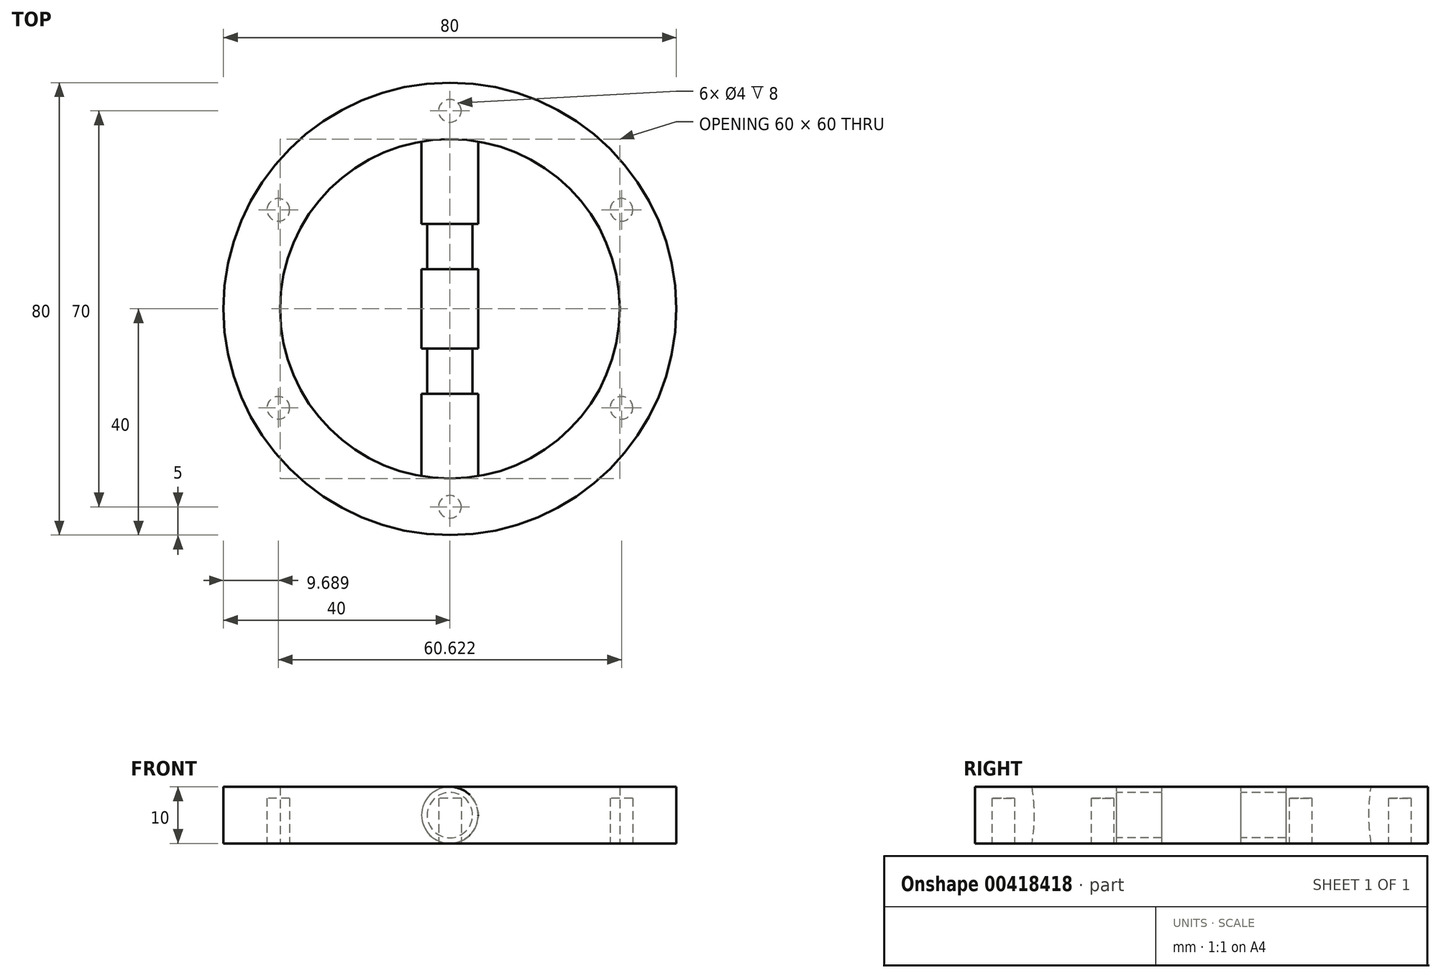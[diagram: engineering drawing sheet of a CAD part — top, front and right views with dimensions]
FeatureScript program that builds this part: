
annotation { "Feature Type Name" : "Feature", "Feature Type Description" : "" }
export const myFeature = defineFeature(function(context is Context, id is Id, definition is map)
    precondition{}
    {
        {
            var Q0;
            Q0=qCreatedBy(makeId("Top.planeOp"),FACE);
            var sketch = newSketch(context, id + "F0", { "sketchPlane" : qUnion([Q0])});
            skCircle(sketch, "E0", {"center": v(0, 0) * mm, "radius": 30 * mm});
            skCircle(sketch, "E1", {"center": v(0, 0) * mm, "radius": 35 * mm, "construction": true});
            skCircle(sketch, "E2", {"center": v(0, 0) * mm, "radius": 40 * mm});
            skLineSegment(sketch, "E3", {"start": v(0, 35) * mm, "end": v(-30.31, -17.5) * mm, "construction": true});
            skLineSegment(sketch, "E4", {"start": v(-30.31, -17.5) * mm, "end": v(30.31, -17.5) * mm, "construction": true});
            skLineSegment(sketch, "E5", {"start": v(30.31, -17.5) * mm, "end": v(0, 35) * mm, "construction": true});
            skLineSegment(sketch, "E6", {"start": v(0, -35) * mm, "end": v(-30.31, 17.5) * mm, "construction": true});
            skLineSegment(sketch, "E7", {"start": v(-30.31, 17.5) * mm, "end": v(30.31, 17.5) * mm, "construction": true});
            skLineSegment(sketch, "E8", {"start": v(30.31, 17.5) * mm, "end": v(0, -35) * mm, "construction": true});
            skCircle(sketch, "E9", {"center": v(0, 35) * mm, "radius": 2 * mm});
            skCircle(sketch, "E10", {"center": v(-30.31, 17.5) * mm, "radius": 2 * mm});
            skCircle(sketch, "E11", {"center": v(-30.31, -17.5) * mm, "radius": 2 * mm});
            skCircle(sketch, "E12", {"center": v(0, -35) * mm, "radius": 2 * mm});
            skCircle(sketch, "E13", {"center": v(30.31, -17.5) * mm, "radius": 2 * mm});
            skCircle(sketch, "E14", {"center": v(30.31, 17.5) * mm, "radius": 2 * mm});
            skSolve(sketch);
        }
        {
            var Q0;
            Q0 = qSketchRegion(id + "F0", true);
            extrude(context, id + "F1", {"entities" : qUnion([Q0]), "depth" : 8 * mm});
        }
        {
            var Q0;
            Q0=makeQuery(id+"F1.opExtrude","CAP_FACE",FACE,{"disambiguationData":[OSD([sQuery(id+"F0.wireOp",EDGE,"E0"),sQuery(id+"F0.wireOp",EDGE,"E2"),sQuery(id+"F0.wireOp",EDGE,"E9"),sQuery(id+"F0.wireOp",EDGE,"E10"),sQuery(id+"F0.wireOp",EDGE,"E11"),sQuery(id+"F0.wireOp",EDGE,"E12"),sQuery(id+"F0.wireOp",EDGE,"E13"),sQuery(id+"F0.wireOp",EDGE,"E14")])],"isStart":false});
            var sketch = newSketch(context, id + "F2", { "sketchPlane" : qUnion([Q0])});
            skCircle(sketch, "E15", {"center": v(0, 0) * mm, "radius": 30 * mm});
            skCircle(sketch, "E16", {"center": v(0, 0) * mm, "radius": 40 * mm});
            skSolve(sketch);
        }
        {
            var Q0;
            Q0 = qSketchRegion(id + "F2", true);
            extrude(context, id + "F3", {"entities" : qUnion([Q0]), "operationType" : NewBodyOperationType.ADD, "depth" : 2 * mm});
        }
        {
            var Q0;
            Q0=qCreatedBy(makeId("Front.planeOp"),FACE);
            var sketch = newSketch(context, id + "F4", { "sketchPlane" : qUnion([Q0])});
            skCircle(sketch, "E17", {"center": v(0, 5) * mm, "radius": 5 * mm});
            skSolve(sketch);
        }
        {
            var Q0;
            Q0 = qSketchRegion(id + "F4", true);
            extrude(context, id + "F5", {"entities" : qUnion([Q0]), "operationType" : NewBodyOperationType.ADD, "endBound" : BoundingType.UP_TO_NEXT, "depth" : 25 * mm, "hasSecondDirection" : true, "secondDirectionBound" : SecondDirectionBoundingType.UP_TO_NEXT, "secondDirectionOppositeDirection" : true, "secondDirectionDepth" : 25 * mm});
        }
        {
            var Q0;
            Q0=qCreatedBy(makeId("Right.planeOp"),FACE);
            var sketch = newSketch(context, id + "F6", { "sketchPlane" : qUnion([Q0])});
            skLineSegment(sketch, "E18.bottom", {"start": v(15, 10) * mm, "end": v(7, 10) * mm});
            skLineSegment(sketch, "E18.top", {"start": v(15, 9) * mm, "end": v(7, 9) * mm});
            skLineSegment(sketch, "E18.left", {"start": v(15, 10) * mm, "end": v(15, 9) * mm});
            skLineSegment(sketch, "E18.right", {"start": v(7, 10) * mm, "end": v(7, 9) * mm});
            skLineSegment(sketch, "E19.bottom", {"start": v(-7, 10) * mm, "end": v(-15, 10) * mm});
            skLineSegment(sketch, "E19.top", {"start": v(-7, 9) * mm, "end": v(-15, 9) * mm});
            skLineSegment(sketch, "E19.left", {"start": v(-7, 10) * mm, "end": v(-7, 9) * mm});
            skLineSegment(sketch, "E19.right", {"start": v(-15, 10) * mm, "end": v(-15, 9) * mm});
            skLineSegment(sketch, "E20", {"start": v(50, 5) * mm, "end": v(-50, 5) * mm, "construction": true});
            skSolve(sketch);
        }
        {
            var Q0;
            Q0 = qSketchRegion(id + "F6", true);
            var Q1;
            Q1=sQuery(id+"F6.wireOp",EDGE,"E20");
            revolve(context, id + "F7", {"operationType" : NewBodyOperationType.REMOVE, "entities" : qUnion([Q0]), "axis" : qUnion([Q1]), "revolveType" : RevolveType.FULL, "oppositeDirection" : true});
        }
    });
